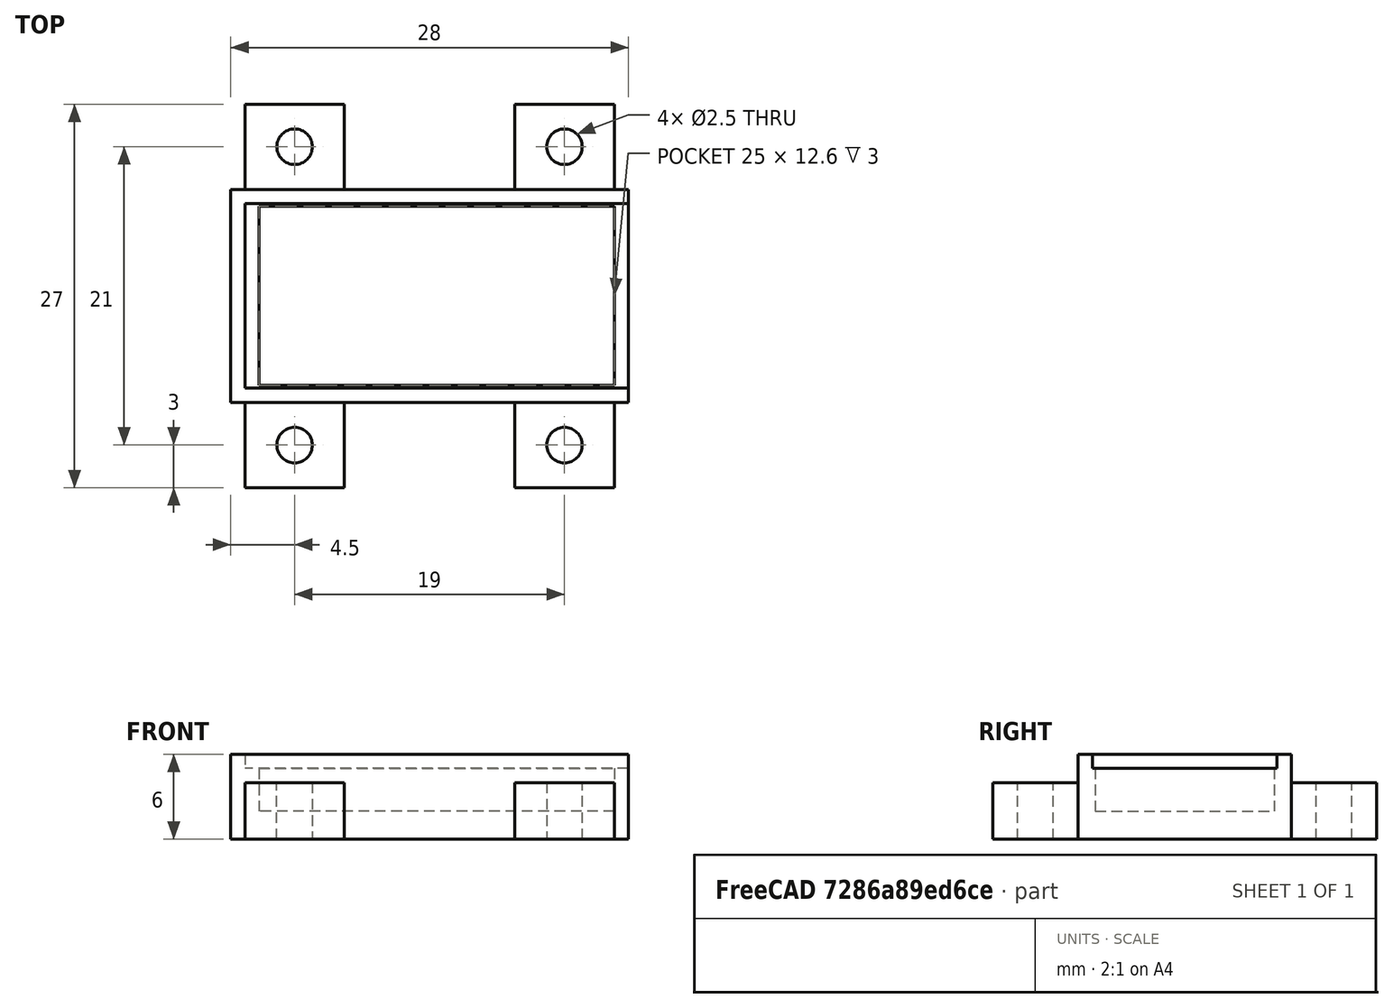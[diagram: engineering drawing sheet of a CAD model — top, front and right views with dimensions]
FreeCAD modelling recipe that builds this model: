
FCSTD DOCUMENT  (FreeCAD 0.19R24267 +99 (Git))
Label: imu_moutning_case
License: All rights reserved
LicenseURL: http://en.wikipedia.org/wiki/All_rights_reserved
objects: Sketcher::SketchObject×5, PartDesign::Pocket×3, PartDesign::Pad×2, PartDesign::Mirrored×2, PartDesign::MultiTransform×1, PartDesign::Body×1, Mesh::Feature×1
note: 19 computed .brp shape members not serialized (recipe doc carries the construction recipe); baked Part::Feature solids carry a one-line shape summary decoded from their .brp

FEATURE [Sketcher::SketchObject] Sketch
  FullyConstrained = false
  MapMode = 5
  Support = -> [XY_Plane]
  sketch-geometry (4):
    g0: LineSegment StartX=-14 StartY=-7.5 StartZ=0 EndX=14 EndY=-7.5 EndZ=0
    g1: LineSegment StartX=14 StartY=-7.5 StartZ=0 EndX=14 EndY=7.5 EndZ=0
    g2: LineSegment StartX=14 StartY=7.5 StartZ=0 EndX=-14 EndY=7.5 EndZ=0
    g3: LineSegment StartX=-14 StartY=7.5 StartZ=0 EndX=-14 EndY=-7.5 EndZ=0
  constraints (8):
    c: Coincident(g0,g1)
    c: Coincident(g1,g2)
    c: Coincident(g2,g3)
    c: Coincident(g3,g0)
    c: Horizontal(g0)
    c: Horizontal(g2)
    c: Vertical(g1)
    c: Vertical(g3)
FEATURE [PartDesign::Pad] Pad
  Direction = (1,1,1)
  Length = 6
  Length2 = 100
  Profile = -> Sketch
  Type = 0
FEATURE [Sketcher::SketchObject] Sketch001
  FullyConstrained = false
  MapMode = 5
  Placement = pos=(0,0,6) rot=(0,0,1;0rad)
  Support = -> [Pad]
  sketch-geometry (4):
    g0: LineSegment StartX=-13 StartY=-6.5 StartZ=0 EndX=14 EndY=-6.5 EndZ=0
    g1: LineSegment StartX=14 StartY=-6.5 StartZ=0 EndX=14 EndY=6.5 EndZ=0
    g2: LineSegment StartX=14 StartY=6.5 StartZ=0 EndX=-13 EndY=6.5 EndZ=0
    g3: LineSegment StartX=-13 StartY=6.5 StartZ=0 EndX=-13 EndY=-6.5 EndZ=0
  constraints (8):
    c: Coincident(g0,g1)
    c: Coincident(g1,g2)
    c: Coincident(g2,g3)
    c: Coincident(g3,g0)
    c: Horizontal(g0)
    c: Horizontal(g2)
    c: Vertical(g1)
    c: Vertical(g3)
FEATURE [PartDesign::Pocket] Pocket  label="PocketShallow"
  BaseFeature = -> Pad
  Length = 1
  Length2 = 100
  Profile = -> Sketch001
  Type = 0
FEATURE [Sketcher::SketchObject] Sketch002
  FullyConstrained = false
  MapMode = 5
  Placement = pos=(0,0,5) rot=(0,0,1;0rad)
  Support = -> [Pocket]
  sketch-geometry (4):
    g0: LineSegment StartX=-12 StartY=6.3 StartZ=0 EndX=13 EndY=6.3 EndZ=0
    g1: LineSegment StartX=13 StartY=6.3 StartZ=0 EndX=13 EndY=-6.3 EndZ=0
    g2: LineSegment StartX=13 StartY=-6.3 StartZ=0 EndX=-12 EndY=-6.3 EndZ=0
    g3: LineSegment StartX=-12 StartY=-6.3 StartZ=0 EndX=-12 EndY=6.3 EndZ=0
  constraints (8):
    c: Coincident(g0,g1)
    c: Coincident(g1,g2)
    c: Coincident(g2,g3)
    c: Coincident(g3,g0)
    c: Horizontal(g0)
    c: Horizontal(g2)
    c: Vertical(g1)
    c: Vertical(g3)
FEATURE [PartDesign::Pocket] Pocket001  label="PocketDeep"
  BaseFeature = -> Pocket
  Length = 3
  Length2 = 100
  Profile = -> Sketch002
  Type = 0
FEATURE [Sketcher::SketchObject] Sketch003
  FullyConstrained = false
  MapMode = 5
  Placement = pos=(0,-7.5,0) rot=(1,0,0;1.5708rad)
  Support = -> [Pocket001]
  sketch-geometry (4):
    g0: LineSegment StartX=-13 StartY=0 StartZ=0 EndX=-6 EndY=0 EndZ=0
    g1: LineSegment StartX=-6 StartY=0 StartZ=0 EndX=-6 EndY=4 EndZ=0
    g2: LineSegment StartX=-6 StartY=4 StartZ=0 EndX=-13 EndY=4 EndZ=0
    g3: LineSegment StartX=-13 StartY=4 StartZ=0 EndX=-13 EndY=0 EndZ=0
  constraints (9):
    c: Coincident(g0,g1)
    c: Coincident(g1,g2)
    c: Coincident(g2,g3)
    c: Coincident(g3,g0)
    c: Horizontal(g0)
    c: Horizontal(g2)
    c: Vertical(g1)
    c: Vertical(g3)
    c: PointOnObject(g0,g-1)
FEATURE [PartDesign::Pad] Pad001  label="Foot"
  BaseFeature = -> Pocket001
  Direction = (1,1,1)
  Length = 6
  Length2 = 100
  Profile = -> Sketch003
  Type = 0
FEATURE [Sketcher::SketchObject] Sketch004
  FullyConstrained = false
  MapMode = 5
  Placement = pos=(0,9e-16,4) rot=(0,0,1;0rad)
  Support = -> [Pad001]
  sketch-geometry (1):
    g0: Circle CenterX=-9.5 CenterY=-10.5 CenterZ=0 NormalX=0 NormalY=0 NormalZ=1 AngleXU=0 Radius=1.25
  constraints (1):
    c: Radius(g0) = 1.25
FEATURE [PartDesign::Pocket] Pocket002  label="FootHole"
  BaseFeature = -> Pad001
  Length = 5
  Length2 = 100
  Profile = -> Sketch004
  Type = 0
FEATURE [PartDesign::Mirrored] Mirrored  label="YZ"
  MirrorPlane = -> YZ_Plane
FEATURE [PartDesign::Mirrored] Mirrored001  label="XZ"
  MirrorPlane = -> XZ_Plane
FEATURE [PartDesign::MultiTransform] MultiTransform  label="MultiTransformFoot"
  BaseFeature = -> Pocket002
  Originals = -> [Pad001,Pocket002]
  Transformations = -> [Mirrored,Mirrored001]
FEATURE [PartDesign::Body] Body
  Group = -> [Sketch,Pad,Sketch001,Pocket,Sketch002,Pocket001,Sketch003,Pad001,Sketch004,Pocket002,MultiTransform,Mirrored,Mirrored001]
  Origin = -> Origin
  Tip = -> MultiTransform
FEATURE [Mesh::Feature] Mesh  label="Body (Meshed)"
